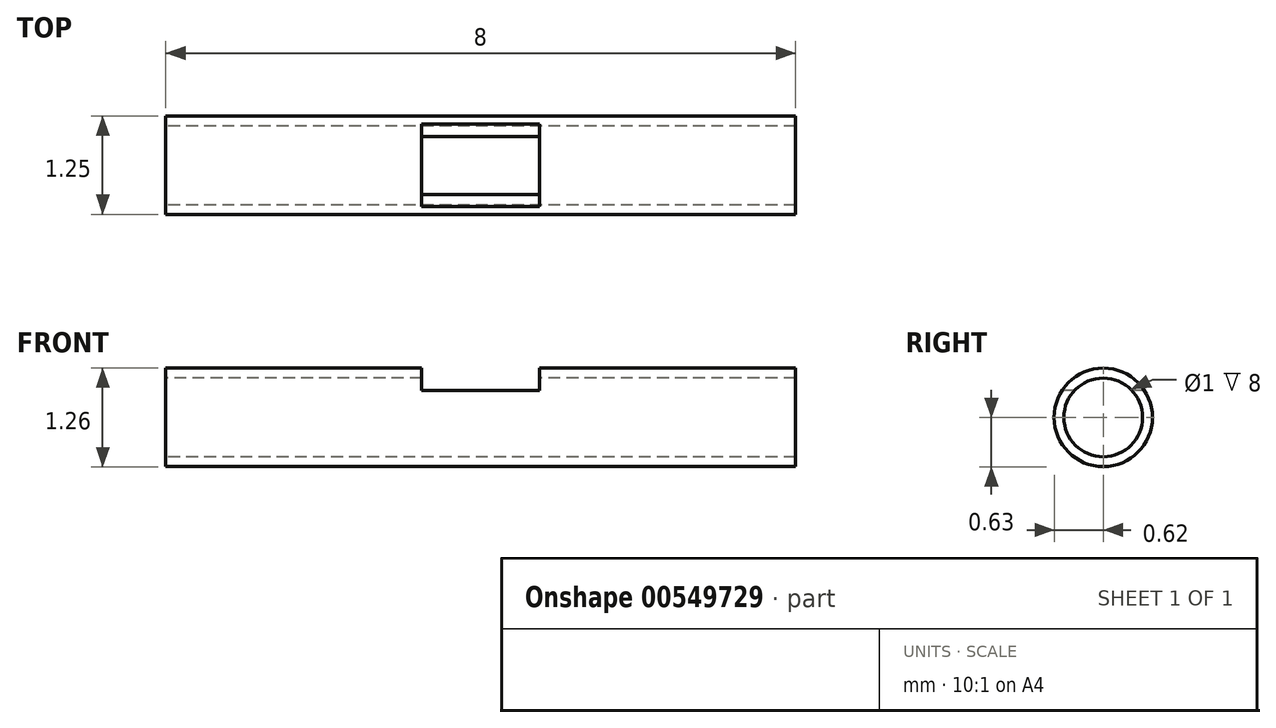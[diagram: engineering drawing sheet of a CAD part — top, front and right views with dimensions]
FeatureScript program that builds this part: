
annotation { "Feature Type Name" : "Feature", "Feature Type Description" : "" }
export const myFeature = defineFeature(function(context is Context, id is Id, definition is map)
    precondition{}
    {
        {
            var Q0;
            Q0=qCreatedBy(makeId("Right.planeOp"),FACE);
            var sketch = newSketch(context, id + "F0", { "sketchPlane" : qUnion([Q0])});
            skCircle(sketch, "E0", {"center": v(-0.08, 0) * mm, "radius": 0.62 * mm});
            skCircle(sketch, "E1", {"center": v(-0.08, 0) * mm, "radius": 0.5 * mm});
            skSolve(sketch);
        }
        {
            var Q0;
            Q0 = qSketchRegion(id + "F0", true);
            extrude(context, id + "F1", {"entities" : qUnion([Q0]), "endBound" : BoundingType.SYMMETRIC, "depth" : 8 * mm, "offsetDistance" : 25 * mm});
        }
        {
            var Q0;
            Q0=qCreatedBy(makeId("Front.planeOp"),FACE);
            var sketch = newSketch(context, id + "F2", { "sketchPlane" : qUnion([Q0])});
            skLineSegment(sketch, "E2.bottom", {"start": v(0.75, 0.34) * mm, "end": v(-0.75, 0.34) * mm});
            skLineSegment(sketch, "E2.top", {"start": v(0.75, 0.84) * mm, "end": v(-0.75, 0.84) * mm});
            skLineSegment(sketch, "E2.left", {"start": v(0.75, 0.34) * mm, "end": v(0.75, 0.84) * mm});
            skLineSegment(sketch, "E2.right", {"start": v(-0.75, 0.34) * mm, "end": v(-0.75, 0.84) * mm});
            skPoint(sketch, "E2.middle", {"position": v(0, 0.6) * mm});
            skSolve(sketch);
        }
        {
            var Q0;
            Q0 = qSketchRegion(id + "F2", true);
            extrude(context, id + "F3", {"entities" : qUnion([Q0]), "operationType" : NewBodyOperationType.REMOVE, "endBound" : BoundingType.SYMMETRIC, "oppositeDirection" : true, "depth" : 2 * mm, "offsetDistance" : 25 * mm});
        }
    });
